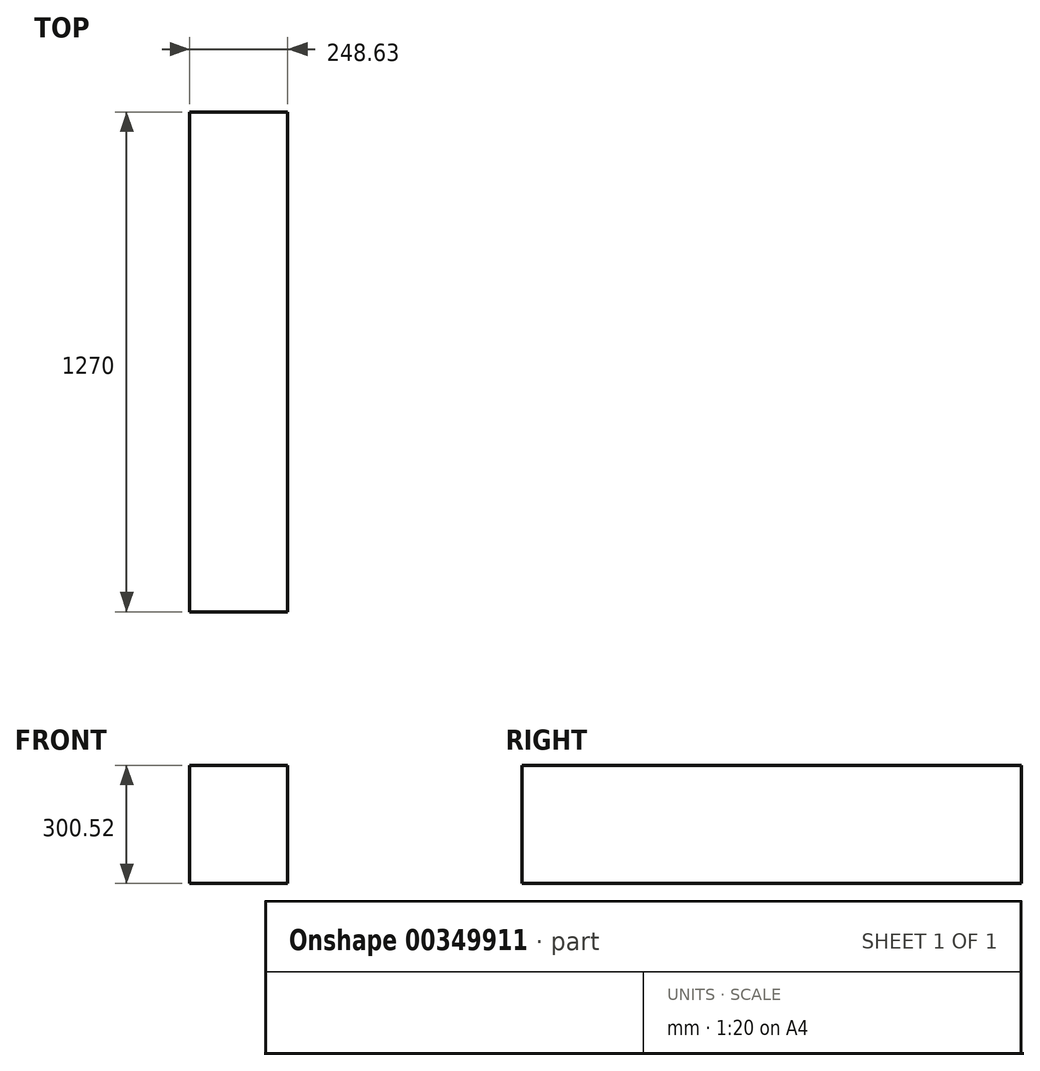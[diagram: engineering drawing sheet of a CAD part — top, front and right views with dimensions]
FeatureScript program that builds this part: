
annotation { "Feature Type Name" : "Feature", "Feature Type Description" : "" }
export const myFeature = defineFeature(function(context is Context, id is Id, definition is map)
    precondition{}
    {
        {
            var Q0;
            Q0=qCreatedBy(makeId("Front.planeOp"),FACE);
            var sketch = newSketch(context, id + "F0", { "sketchPlane" : qUnion([Q0])});
            skLineSegment(sketch, "E0.bottom", {"start": v(-107.95, 213.1) * mm, "end": v(140.68, 213.1) * mm});
            skLineSegment(sketch, "E0.top", {"start": v(-107.95, -87.4) * mm, "end": v(140.68, -87.4) * mm});
            skLineSegment(sketch, "E0.left", {"start": v(-107.95, 213.1) * mm, "end": v(-107.95, -87.4) * mm});
            skLineSegment(sketch, "E0.right", {"start": v(140.68, 213.1) * mm, "end": v(140.68, -87.4) * mm});
            skSolve(sketch);
        }
        {
            var Q0;
            Q0 = qSketchRegion(id + "F0", true);
            extrude(context, id + "F1", {"entities" : qUnion([Q0]), "depth" : 1270 * mm});
        }
    });
